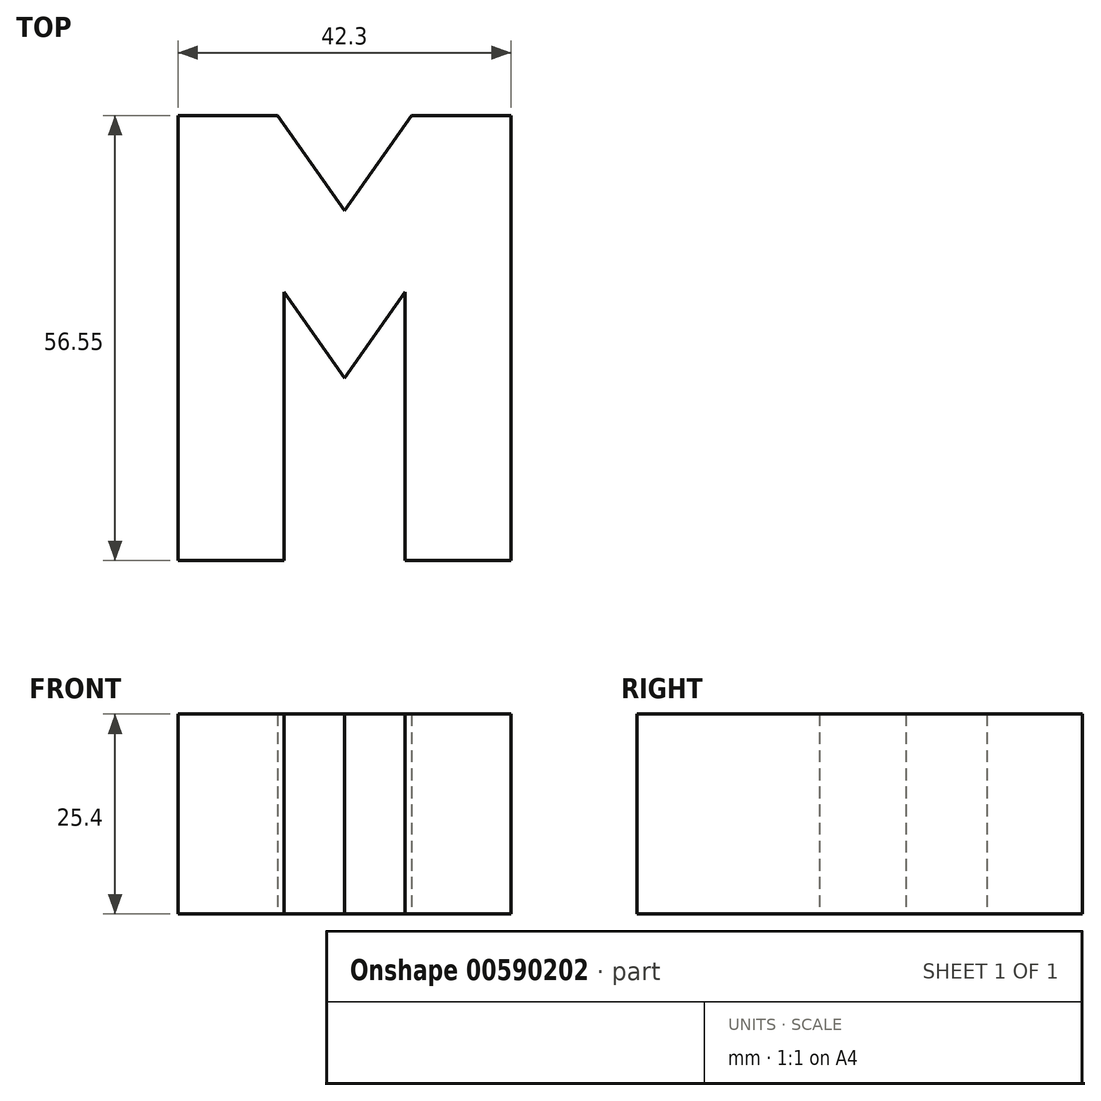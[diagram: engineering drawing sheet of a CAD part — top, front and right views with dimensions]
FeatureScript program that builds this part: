
annotation { "Feature Type Name" : "Feature", "Feature Type Description" : "" }
export const myFeature = defineFeature(function(context is Context, id is Id, definition is map)
    precondition{}
    {
        {
            var Q0;
            Q0=qCreatedBy(makeId("Top.planeOp"),FACE);
            var sketch = newSketch(context, id + "F0", { "sketchPlane" : qUnion([Q0])});
            skLineSegment(sketch, "E0", {"start": v(-27.62, 0) * mm, "end": v(-27.62, 52.13) * mm});
            skLineSegment(sketch, "E1.MirrorCS", {"start": v(27.62, 0) * mm, "end": v(27.62, 52.13) * mm});
            skLineSegment(sketch, "E2", {"start": v(-27.62, 0) * mm, "end": v(-14.92, 0) * mm});
            skLineSegment(sketch, "E3.MirrorCS", {"start": v(27.62, 0) * mm, "end": v(14.92, 0) * mm});
            skLineSegment(sketch, "E4", {"start": v(-27.62, 0) * mm, "end": v(-27.62, 66.63) * mm});
            skLineSegment(sketch, "E5", {"start": v(27.62, 52.13) * mm, "end": v(27.62, 64.61) * mm});
            skLineSegment(sketch, "E6", {"start": v(-27.62, 66.63) * mm, "end": v(27.49, 66.63) * mm});
            skLineSegment(sketch, "E7", {"start": v(27.49, 66.63) * mm, "end": v(27.62, 0) * mm});
            skLineSegment(sketch, "E8", {"start": v(-14.92, 0) * mm, "end": v(-14.92, 52.24) * mm});
            skLineSegment(sketch, "E9.MirrorCS", {"start": v(14.92, 0) * mm, "end": v(14.92, 52.24) * mm});
            skLineSegment(sketch, "E10", {"start": v(-14.92, 52.24) * mm, "end": v(14.92, 52.24) * mm});
            skLineSegment(sketch, "E11", {"start": v(-14.92, 30.94) * mm, "end": v(14.92, 30.94) * mm});
            skLineSegment(sketch, "E12", {"start": v(-14.92, 21.73) * mm, "end": v(14.92, 21.73) * mm});
            skSolve(sketch);
        }
        {
            var Q0;
            Q0 = qSketchRegion(id + "F0", true);
            extrude(context, id + "F1", {"entities" : qUnion([Q0]), "depth" : 25.4 * mm, "offsetDistance" : 25.4 * mm});
        }
        {
            var Q0;
            Q0=makeQuery(id+"F1.opExtrude","SWEPT_FACE",FACE,{"disambiguationData":[OSD([sQuery(id+"F0.wireOp",EDGE,"E7")])]});
            var Q1;
            Q1=makeQuery(id+"F1.opExtrude","CAP_EDGE",EDGE,{"disambiguationData":[OSD([sQuery(id+"F0.wireOp",EDGE,"E6")])],"isStart":true});
            var Q2;
            Q2=makeQuery(id+"F1.opExtrude","SWEPT_EDGE",EDGE,{"disambiguationData":[OSD([sQuery(id+"F0.wireOp",EDGE,"E4"),sQuery(id+"F0.wireOp",EDGE,"E6")])]});
            var Q3;
            {var subQ0=sQuery(id+"F0.wireOp",EDGE,"E8");Q3=makeQuery(id+"F1.opExtrude","SWEPT_FACE",FACE,{"disambiguationData":[OSD([subQ0]),TDD([makeQuery(id+"F0.imprint","IMPRINT",EDGE,{"disambiguationData":[TD([[makeQuery(id+"F0.imprint","INTERSECT",VERTEX,{"derivedFrom":[subQ0,sQuery(id+"F0.wireOp",EDGE,"E10")]}),1.0]])],"derivedFrom":subQ0})])]});}
            var Q4;
            Q4=makeQuery(id+"F1.opExtrude","CAP_FACE",FACE,{"disambiguationData":[OSD([sQuery(id+"F0.wireOp",EDGE,"E2"),sQuery(id+"F0.wireOp",EDGE,"E3.MirrorCS"),sQuery(id+"F0.wireOp",EDGE,"E4"),sQuery(id+"F0.wireOp",EDGE,"E6"),sQuery(id+"F0.wireOp",EDGE,"E7"),sQuery(id+"F0.wireOp",EDGE,"E8"),sQuery(id+"F0.wireOp",EDGE,"E9.MirrorCS"),sQuery(id+"F0.wireOp",EDGE,"E10"),sQuery(id+"F0.wireOp",EDGE,"E11"),sQuery(id+"F0.wireOp",EDGE,"E12")])],"isStart":false});
            var Q5;
            {var subQ0=sQuery(id+"F0.wireOp",EDGE,"E9.MirrorCS");Q5=makeQuery(id+"F1.opExtrude","SWEPT_FACE",FACE,{"disambiguationData":[OSD([subQ0]),TDD([makeQuery(id+"F0.imprint","IMPRINT",EDGE,{"disambiguationData":[TD([[makeQuery(id+"F0.imprint","INTERSECT",VERTEX,{"derivedFrom":[subQ0,sQuery(id+"F0.wireOp",EDGE,"E10")]}),1.0]])],"derivedFrom":subQ0})])]});}
            var Q6;
            {var subQ0=sQuery(id+"F0.wireOp",EDGE,"E9.MirrorCS");Q6=makeQuery(id+"F1.opExtrude","SWEPT_FACE",FACE,{"disambiguationData":[OSD([subQ0]),TDD([makeQuery(id+"F0.imprint","IMPRINT",EDGE,{"disambiguationData":[TD([[makeQuery(id+"F0.imprint","INTERSECT",VERTEX,{"derivedFrom":[sQuery(id+"F0.wireOp",EDGE,"E3.MirrorCS"),subQ0]}),-1.0]])],"derivedFrom":subQ0})])]});}
            var Q7;
            {var subQ0=sQuery(id+"F0.wireOp",EDGE,"E8");Q7=makeQuery(id+"F1.opExtrude","SWEPT_FACE",FACE,{"disambiguationData":[OSD([subQ0]),TDD([makeQuery(id+"F0.imprint","IMPRINT",EDGE,{"disambiguationData":[TD([[makeQuery(id+"F0.imprint","INTERSECT",VERTEX,{"derivedFrom":[sQuery(id+"F0.wireOp",EDGE,"E2"),subQ0]}),-1.0]])],"derivedFrom":subQ0})])]});}
            var Q8;
            Q8=makeQuery(id+"F1.opExtrude","SWEPT_FACE",FACE,{"disambiguationData":[OSD([sQuery(id+"F0.wireOp",EDGE,"E2")])]});
            var Q9;
            Q9=makeQuery(id+"F1.opExtrude","CAP_FACE",FACE,{"disambiguationData":[OSD([sQuery(id+"F0.wireOp",EDGE,"E2"),sQuery(id+"F0.wireOp",EDGE,"E3.MirrorCS"),sQuery(id+"F0.wireOp",EDGE,"E4"),sQuery(id+"F0.wireOp",EDGE,"E6"),sQuery(id+"F0.wireOp",EDGE,"E7"),sQuery(id+"F0.wireOp",EDGE,"E8"),sQuery(id+"F0.wireOp",EDGE,"E9.MirrorCS"),sQuery(id+"F0.wireOp",EDGE,"E10"),sQuery(id+"F0.wireOp",EDGE,"E11"),sQuery(id+"F0.wireOp",EDGE,"E12")])],"isStart":true});
            var Q10;
            Q10=makeQuery(id+"F1.opExtrude","SWEPT_FACE",FACE,{"disambiguationData":[OSD([sQuery(id+"F0.wireOp",EDGE,"E4")])]});
            fillet(context, id + "F2", {"entities" : qUnion([Q0, Q1, Q2, Q3, Q4, Q5, Q6, Q7, Q8, Q9, Q10]), "radius" : 5.08 * mm, "tangentPropagation" : true, "allowEdgeOverflow" : false});
        }
        {
            var Q0;
            Q0=makeQuery(id+"F1.opExtrude","CAP_FACE",FACE,{"disambiguationData":[OSD([sQuery(id+"F0.wireOp",EDGE,"E2"),sQuery(id+"F0.wireOp",EDGE,"E3.MirrorCS"),sQuery(id+"F0.wireOp",EDGE,"E4"),sQuery(id+"F0.wireOp",EDGE,"E6"),sQuery(id+"F0.wireOp",EDGE,"E7"),sQuery(id+"F0.wireOp",EDGE,"E8"),sQuery(id+"F0.wireOp",EDGE,"E9.MirrorCS"),sQuery(id+"F0.wireOp",EDGE,"E10"),sQuery(id+"F0.wireOp",EDGE,"E11"),sQuery(id+"F0.wireOp",EDGE,"E12")])],"isStart":false});
            extrude(context, id + "F3", {"entities" : qUnion([Q0]), "operationType" : NewBodyOperationType.ADD, "depth" : 25.4 * mm, "offsetDistance" : 25.4 * mm});
        }
        {
            var Q0;
            Q0=makeQuery(id+"F1.opExtrude","SWEPT_BODY",BODY,{"disambiguationData":[OSD([sQuery(id+"F0.wireOp",EDGE,"E2"),sQuery(id+"F0.wireOp",EDGE,"E3.MirrorCS"),sQuery(id+"F0.wireOp",EDGE,"E4"),sQuery(id+"F0.wireOp",EDGE,"E6"),sQuery(id+"F0.wireOp",EDGE,"E7"),sQuery(id+"F0.wireOp",EDGE,"E8"),sQuery(id+"F0.wireOp",EDGE,"E9.MirrorCS"),sQuery(id+"F0.wireOp",EDGE,"E10"),sQuery(id+"F0.wireOp",EDGE,"E11"),sQuery(id+"F0.wireOp",EDGE,"E12")])]});
            deleteBodies(context, id + "F4", {"entities" : qUnion([Q0])});
        }
        {
            var Q0;
            Q0=qCreatedBy(makeId("Top.planeOp"),FACE);
            var sketch = newSketch(context, id + "F5", { "sketchPlane" : qUnion([Q0])});
            skLineSegment(sketch, "E13", {"start": v(-21.15, 56.55) * mm, "end": v(-21.15, 0) * mm});
            skLineSegment(sketch, "E14", {"start": v(-21.15, 56.55) * mm, "end": v(-8.5, 56.55) * mm});
            skLineSegment(sketch, "E15", {"start": v(-21.15, 0) * mm, "end": v(-7.7, 0) * mm});
            skLineSegment(sketch, "E16", {"start": v(0, 56.55) * mm, "end": v(0, -5.32) * mm});
            skLineSegment(sketch, "E17.MirrorCS", {"start": v(21.15, 56.55) * mm, "end": v(8.5, 56.55) * mm});
            skLineSegment(sketch, "E18.MirrorCS", {"start": v(21.15, 56.55) * mm, "end": v(21.15, 0) * mm});
            skLineSegment(sketch, "E19.MirrorCS", {"start": v(21.15, 0) * mm, "end": v(7.7, 0) * mm});
            skLineSegment(sketch, "E20", {"start": v(-7.7, 0) * mm, "end": v(-7.7, 34.13) * mm});
            skLineSegment(sketch, "E21", {"start": v(-7.7, 34.13) * mm, "end": v(0, 23.17) * mm});
            skLineSegment(sketch, "E22.MirrorCS", {"start": v(7.7, 34.13) * mm, "end": v(0, 23.17) * mm});
            skLineSegment(sketch, "E23.MirrorCS", {"start": v(7.7, 0) * mm, "end": v(7.7, 34.13) * mm});
            skLineSegment(sketch, "E24", {"start": v(-8.5, 56.55) * mm, "end": v(0, 44.47) * mm});
            skLineSegment(sketch, "E25", {"start": v(0, 44.47) * mm, "end": v(8.5, 56.55) * mm});
            skSolve(sketch);
        }
        {
            var Q0;
            Q0 = qSketchRegion(id + "F5", true);
            extrude(context, id + "F6", {"entities" : qUnion([Q0]), "depth" : 25.4 * mm, "offsetDistance" : 25.4 * mm});
        }
    });
